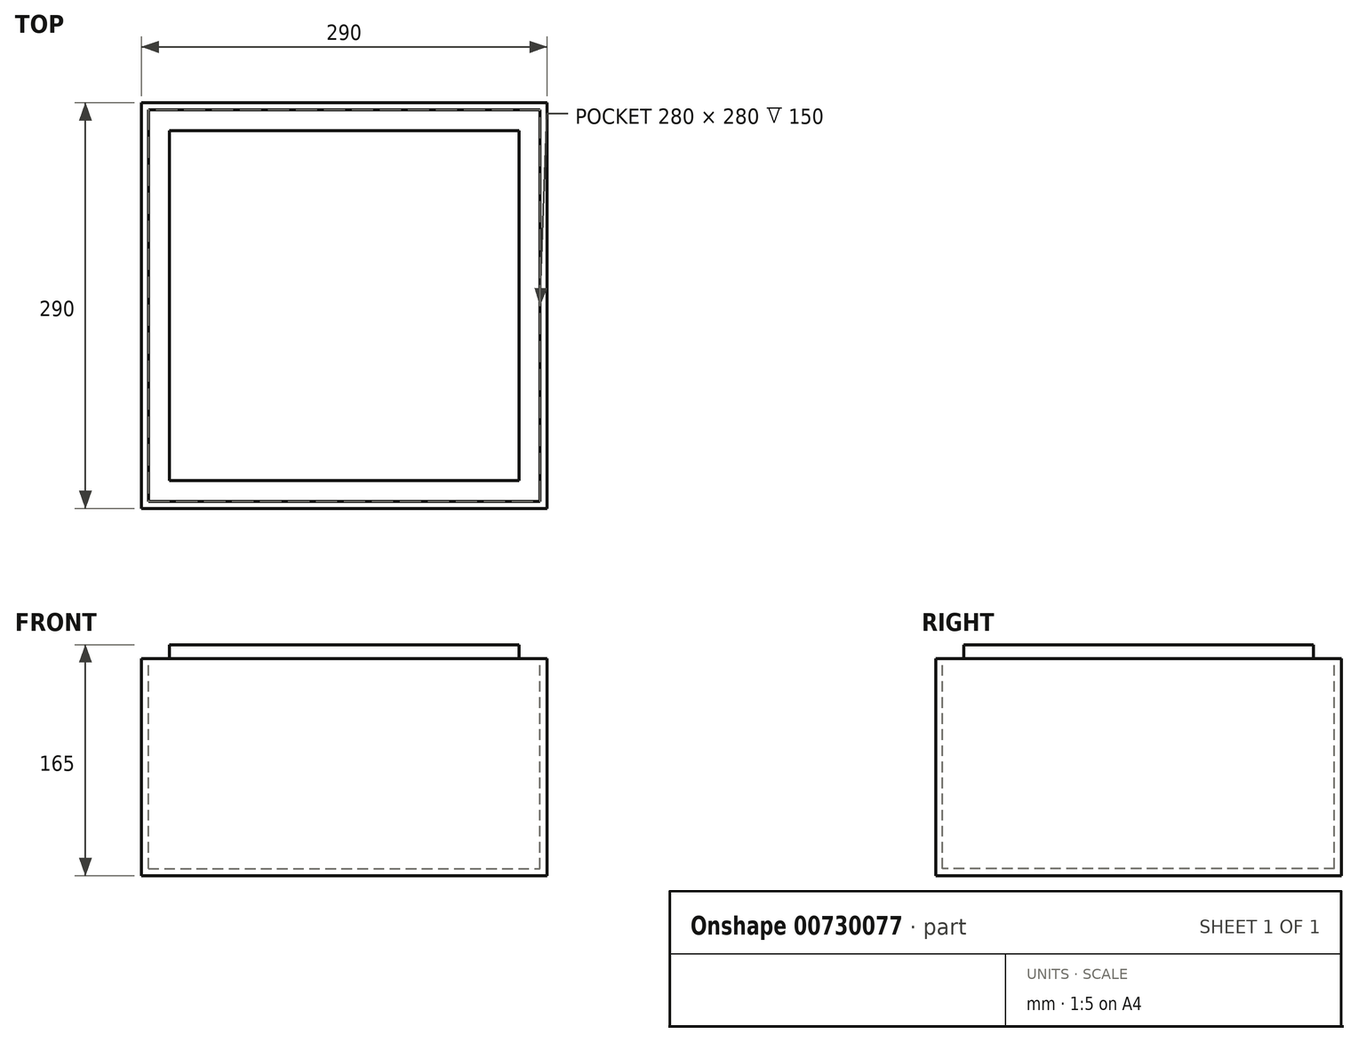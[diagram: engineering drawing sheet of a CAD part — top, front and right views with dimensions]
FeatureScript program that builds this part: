
annotation { "Feature Type Name" : "Feature", "Feature Type Description" : "" }
export const myFeature = defineFeature(function(context is Context, id is Id, definition is map)
    precondition{}
    {
        {
            var Q0;
            Q0=qCreatedBy(makeId("Top.planeOp"),FACE);
            var sketch = newSketch(context, id + "F0", { "sketchPlane" : qUnion([Q0])});
            skLineSegment(sketch, "E0.bottom", {"start": v(-125, 125) * mm, "end": v(125, 125) * mm});
            skLineSegment(sketch, "E0.top", {"start": v(-125, -125) * mm, "end": v(125, -125) * mm});
            skLineSegment(sketch, "E0.left", {"start": v(-125, 125) * mm, "end": v(-125, -125) * mm});
            skLineSegment(sketch, "E0.right", {"start": v(125, 125) * mm, "end": v(125, -125) * mm});
            skSolve(sketch);
        }
        {
            var Q0;
            Q0 = qSketchRegion(id + "F0", true);
            extrude(context, id + "F1", {"entities" : qUnion([Q0]), "depth" : 10 * mm, "offsetDistance" : 25 * mm});
        }
        {
            var Q0;
            Q0=qCreatedBy(makeId("Top.planeOp"),FACE);
            var sketch = newSketch(context, id + "F2", { "sketchPlane" : qUnion([Q0])});
            skLineSegment(sketch, "E1.bottom", {"start": v(-140, 140) * mm, "end": v(140, 140) * mm});
            skLineSegment(sketch, "E1.top", {"start": v(-140, -140) * mm, "end": v(140, -140) * mm});
            skLineSegment(sketch, "E1.left", {"start": v(-140, 140) * mm, "end": v(-140, -140) * mm});
            skLineSegment(sketch, "E1.right", {"start": v(140, 140) * mm, "end": v(140, -140) * mm});
            skLineSegment(sketch, "E2.0", {"start": v(-145, 145) * mm, "end": v(-145, -145) * mm});
            skLineSegment(sketch, "E2.1", {"start": v(-145, 145) * mm, "end": v(145, 145) * mm});
            skLineSegment(sketch, "E2.2", {"start": v(145, 145) * mm, "end": v(145, -145) * mm});
            skLineSegment(sketch, "E2.3", {"start": v(-145, -145) * mm, "end": v(145, -145) * mm});
            skSolve(sketch);
        }
        {
            var Q0;
            Q0=makeQuery(id+"F2.imprint","IMPRINT",FACE,{"disambiguationData":[TD([[makeQuery(id+"F2.imprint","IMPRINT",EDGE,{"derivedFrom":sQuery(id+"F2.wireOp",EDGE,"E1.bottom")}),1.0]])]});
            extrude(context, id + "F3", {"entities" : qUnion([Q0]), "oppositeDirection" : true, "depth" : 150 * mm, "offsetDistance" : 25 * mm});
        }
        {
            var Q0;
            Q0=makeQuery(id+"F3.opExtrude","CAP_FACE",FACE,{"disambiguationData":[OSD([sQuery(id+"F2.wireOp",EDGE,"E1.bottom"),sQuery(id+"F2.wireOp",EDGE,"E1.top"),sQuery(id+"F2.wireOp",EDGE,"E1.left"),sQuery(id+"F2.wireOp",EDGE,"E1.right"),sQuery(id+"F2.wireOp",EDGE,"E2.0"),sQuery(id+"F2.wireOp",EDGE,"E2.1"),sQuery(id+"F2.wireOp",EDGE,"E2.2"),sQuery(id+"F2.wireOp",EDGE,"E2.3")])],"isStart":false});
            var sketch = newSketch(context, id + "F4", { "sketchPlane" : qUnion([Q0])});
            skLineSegment(sketch, "E3.0", {"start": v(-145, -145) * mm, "end": v(-145, 145) * mm});
            skLineSegment(sketch, "E4.0", {"start": v(-145, 145) * mm, "end": v(145, 145) * mm});
            skLineSegment(sketch, "E5.0", {"start": v(145, -145) * mm, "end": v(145, 145) * mm});
            skLineSegment(sketch, "E6.0", {"start": v(-145, -145) * mm, "end": v(145, -145) * mm});
            skSolve(sketch);
        }
        {
            var Q0;
            Q0=makeQuery(id+"F4.imprint","IMPRINT",FACE,{"disambiguationData":[TD([[makeQuery(id+"F4.imprint","IMPRINT",EDGE,{"derivedFrom":sQuery(id+"F4.wireOp",EDGE,"E3.0")}),-1.0]])]});
            var Q1;
            Q1=makeQuery(id+"F4.imprint","IMPRINT",FACE,{"disambiguationData":[TD([[makeQuery(id+"F4.imprint","IMPRINT",EDGE,{"derivedFrom":makeQuery(id+"F3.opExtrude","CAP_EDGE",EDGE,{"disambiguationData":[OSD([sQuery(id+"F2.wireOp",EDGE,"E1.bottom")])],"isStart":false})}),1.0]])]});
            extrude(context, id + "F5", {"entities" : qUnion([Q0, Q1]), "operationType" : NewBodyOperationType.ADD, "depth" : 5 * mm, "offsetDistance" : 25 * mm});
        }
    });
